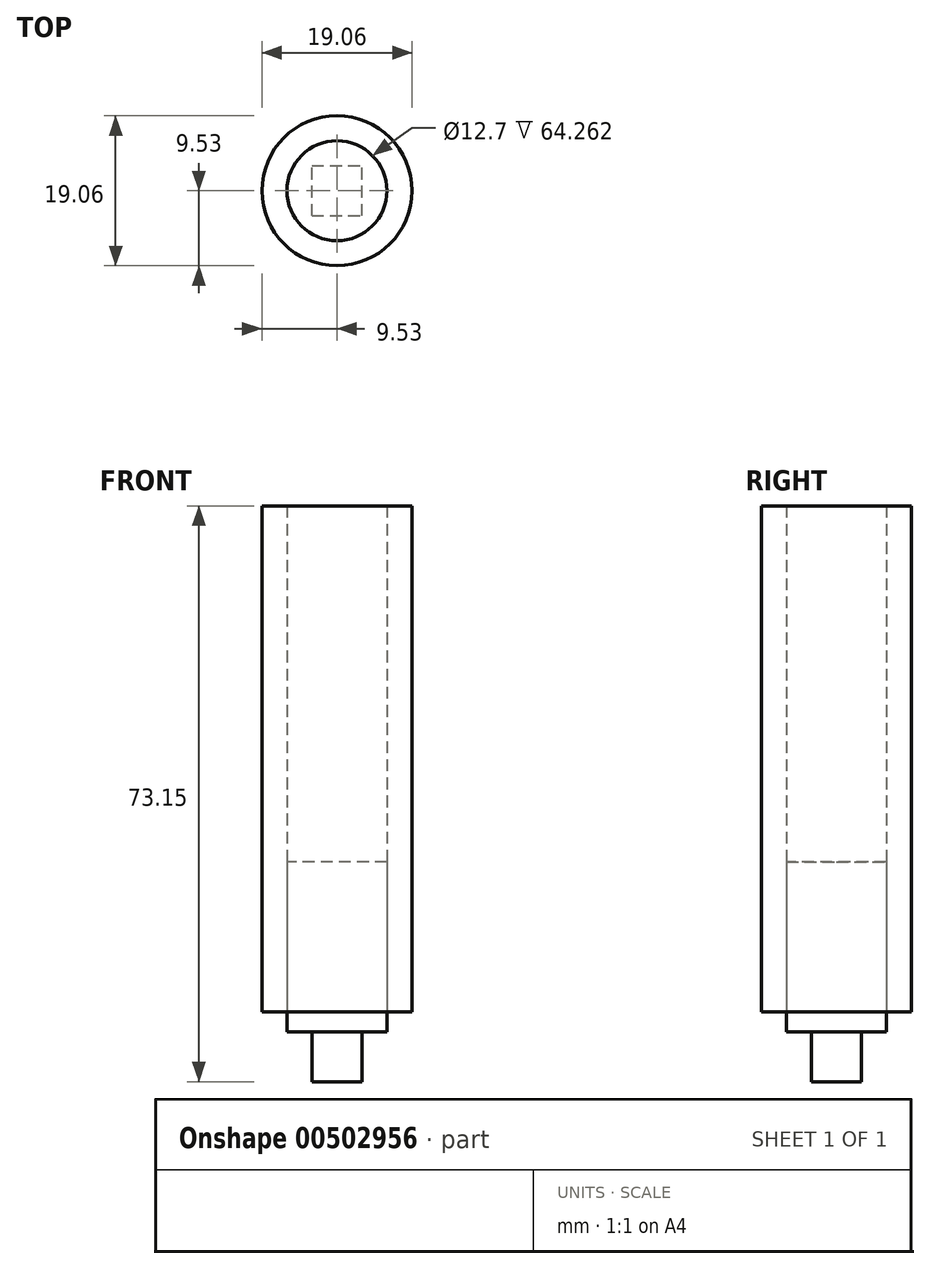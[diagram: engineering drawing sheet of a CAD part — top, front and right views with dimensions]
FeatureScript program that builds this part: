
annotation { "Feature Type Name" : "Feature", "Feature Type Description" : "" }
export const myFeature = defineFeature(function(context is Context, id is Id, definition is map)
    precondition{}
    {
        {
            var Q0;
            Q0=qCreatedBy(makeId("Top.planeOp"),FACE);
            var sketch = newSketch(context, id + "F0", { "sketchPlane" : qUnion([Q0])});
            skCircle(sketch, "E0", {"center": v(0, 0) * mm, "radius": 9.53 * mm});
            skCircle(sketch, "E1", {"center": v(0, 0) * mm, "radius": 6.35 * mm});
            skSolve(sketch);
        }
        {
            var Q0;
            Q0=makeQuery(id+"F0.imprint","IMPRINT",FACE,{"disambiguationData":[TD([[makeQuery(id+"F0.imprint","IMPRINT",EDGE,{"derivedFrom":sQuery(id+"F0.wireOp",EDGE,"E0")}),1.0]])]});
            extrude(context, id + "F1", {"entities" : qUnion([Q0]), "depth" : 64.26 * mm});
        }
        {
            var Q0;
            Q0=makeQuery(id+"F1.opExtrude","CAP_FACE",FACE,{"disambiguationData":[OSD([sQuery(id+"F0.wireOp",EDGE,"E0")])],"isStart":false});
            var sketch = newSketch(context, id + "F2", { "sketchPlane" : qUnion([Q0])});
            skCircle(sketch, "E2", {"center": v(0, 0) * mm, "radius": 6.35 * mm});
            skSolve(sketch);
        }
        {
            var Q0;
            Q0=makeQuery(id+"F2.imprint","IMPRINT",FACE,{"disambiguationData":[TD([[makeQuery(id+"F2.imprint","IMPRINT",EDGE,{"derivedFrom":sQuery(id+"F2.wireOp",EDGE,"E2")}),1.0]])]});
            extrude(context, id + "F3", {"entities" : qUnion([Q0]), "operationType" : NewBodyOperationType.REMOVE, "oppositeDirection" : true, "depth" : 63.5 * mm});
        }
        {
            var Q0;
            Q0=makeQuery(id+"F0.imprint","IMPRINT",FACE,{"disambiguationData":[TD([[makeQuery(id+"F0.imprint","IMPRINT",EDGE,{"derivedFrom":sQuery(id+"F0.wireOp",EDGE,"E1")}),1.0]])]});
            extrude(context, id + "F4", {"entities" : qUnion([Q0]), "depth" : 19.05 * mm, "hasSecondDirection" : true, "secondDirectionOppositeDirection" : true, "secondDirectionDepth" : 2.54 * mm});
        }
        {
            var Q0;
            Q0=makeQuery(id+"F4.opExtrude","CAP_FACE",FACE,{"disambiguationData":[OSD([sQuery(id+"F0.wireOp",EDGE,"E1")])],"isStart":true});
            var sketch = newSketch(context, id + "F5", { "sketchPlane" : qUnion([Q0])});
            skLineSegment(sketch, "E3.bottom", {"start": v(-3.17, 3.17) * mm, "end": v(3.18, 3.18) * mm});
            skLineSegment(sketch, "E3.top", {"start": v(-3.18, -3.18) * mm, "end": v(3.18, -3.18) * mm});
            skLineSegment(sketch, "E3.left", {"start": v(-3.17, 3.17) * mm, "end": v(-3.17, -3.18) * mm});
            skLineSegment(sketch, "E3.right", {"start": v(3.18, 3.18) * mm, "end": v(3.18, -3.18) * mm});
            skSolve(sketch);
        }
        {
            var Q0;
            Q0=makeQuery(id+"F5.imprint","IMPRINT",FACE,{"disambiguationData":[TD([[makeQuery(id+"F5.imprint","IMPRINT",EDGE,{"derivedFrom":sQuery(id+"F5.wireOp",EDGE,"E3.bottom")}),-1.0]])]});
            extrude(context, id + "F6", {"entities" : qUnion([Q0]), "operationType" : NewBodyOperationType.ADD, "depth" : 6.35 * mm});
        }
    });
